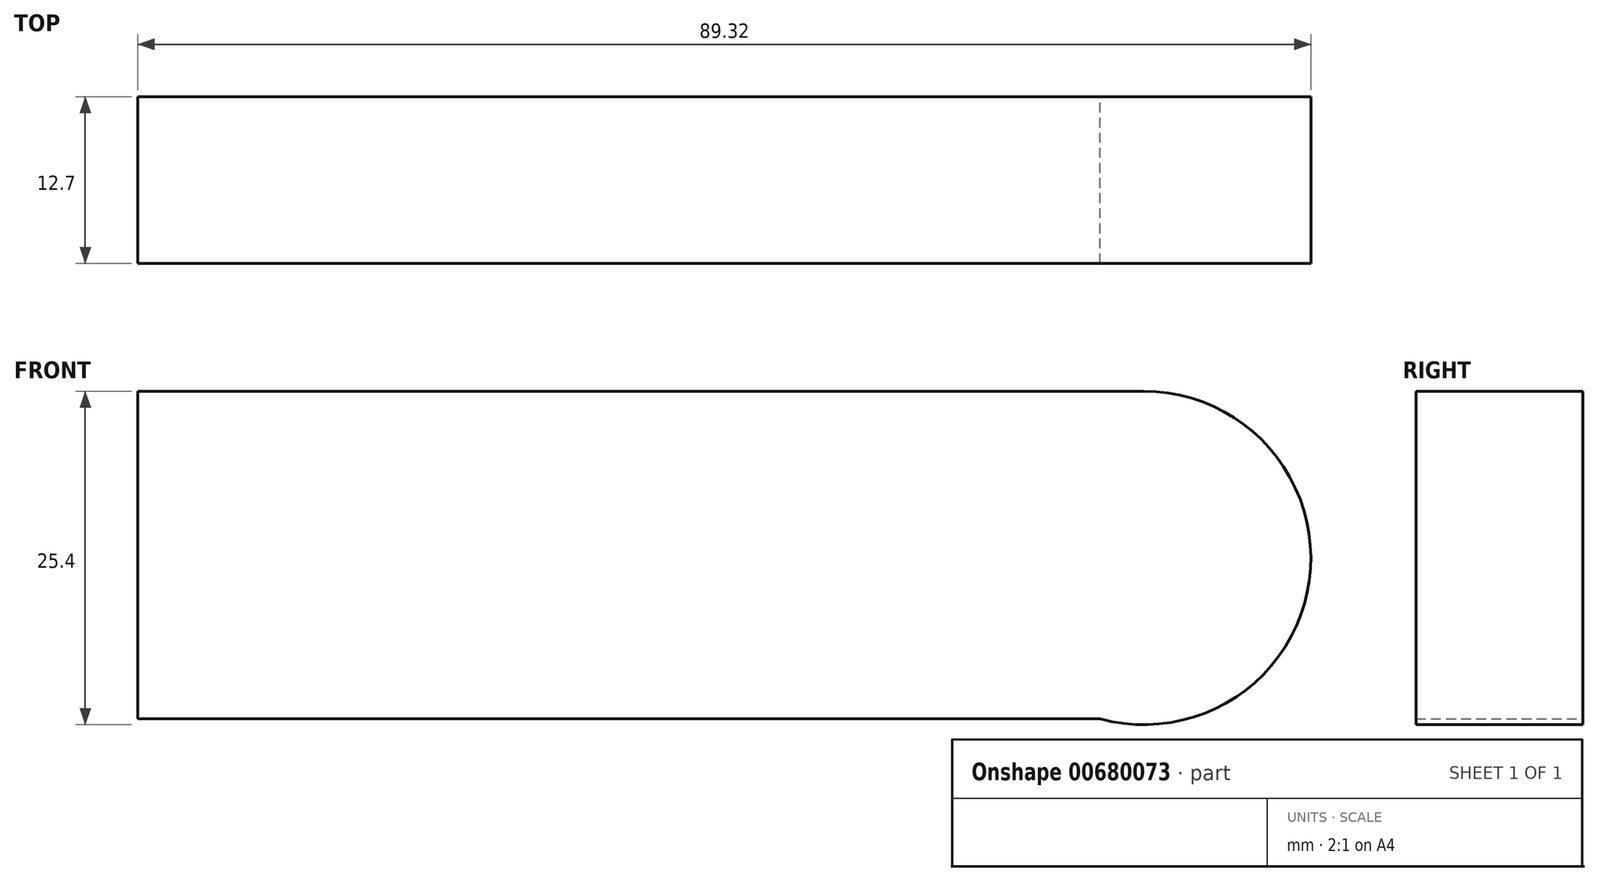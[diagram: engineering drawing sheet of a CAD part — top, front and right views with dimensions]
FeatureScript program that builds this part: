
annotation { "Feature Type Name" : "Feature", "Feature Type Description" : "" }
export const myFeature = defineFeature(function(context is Context, id is Id, definition is map)
    precondition{}
    {
        {
            var Q0;
            Q0=qCreatedBy(makeId("Front.planeOp"),FACE);
            var sketch = newSketch(context, id + "F0", { "sketchPlane" : qUnion([Q0])});
            skCircle(sketch, "E0", {"center": v(0, 0) * mm, "radius": 12.7 * mm});
            skLineSegment(sketch, "E1.bottom", {"start": v(0, 12.7) * mm, "end": v(-76.62, 12.7) * mm});
            skLineSegment(sketch, "E1.top", {"start": v(0, -12.25) * mm, "end": v(-76.62, -12.25) * mm});
            skLineSegment(sketch, "E1.left", {"start": v(0, 12.7) * mm, "end": v(0, -12.25) * mm});
            skLineSegment(sketch, "E1.right", {"start": v(-76.62, 12.7) * mm, "end": v(-76.62, -12.25) * mm});
            skPoint(sketch, "E2.orphan", {"position": v(-76.62, -43) * mm});
            skSolve(sketch);
        }
        {
            var Q0;
            {var subQ0=sQuery(id+"F0.wireOp",EDGE,"E1.bottom");Q0=makeQuery(id+"F0.imprint","IMPRINT",FACE,{"disambiguationData":[TD([[makeQuery(id+"F0.imprint","IMPRINT",EDGE,{"derivedFrom":subQ0}),1.0]])]});}
            var Q1;
            {var subQ0=sQuery(id+"F0.wireOp",EDGE,"E1.left");Q1=makeQuery(id+"F0.imprint","IMPRINT",FACE,{"disambiguationData":[TD([[makeQuery(id+"F0.imprint","IMPRINT",EDGE,{"derivedFrom":subQ0}),-1.0]])]});}
            var Q2;
            {var subQ0=sQuery(id+"F0.wireOp",EDGE,"E1.left");Q2=makeQuery(id+"F0.imprint","IMPRINT",FACE,{"disambiguationData":[TD([[makeQuery(id+"F0.imprint","IMPRINT",EDGE,{"derivedFrom":subQ0}),1.0]])]});}
            extrude(context, id + "F1", {"entities" : qUnion([Q0, Q1, Q2]), "depth" : 12.7 * mm, "offsetDistance" : 25.4 * mm});
        }
    });
